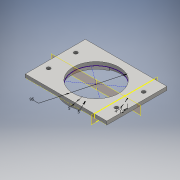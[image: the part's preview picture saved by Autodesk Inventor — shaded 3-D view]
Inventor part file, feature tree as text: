
AUTODESK INVENTOR PART (.ipt)
format: ipt  version: 2016 (Build 200138000, 138)  size: 188,928 bytes
history: native  units: mm
features: extrude x6, sketch x4, plane x2, other x1, revolve x1, chamfer x1, projected_geometry x1
ambient origin geometry x8: Origin, YZ Plane, XZ Plane, XY Plane, X Axis, Y Axis, Z Axis, Center Point
bodies: Solid1 (feature_tree)
feature tree (16):
  sketch  "Sketch1"  dims[d1=126.6mm d2=50.7mm]
  extrude  "Extrusion1"  Depth=50.7mm
  sketch  "Sketch4"  dims[d3=6.75mm d4=152.0mm]
  extrude  "Extrusion2"  Depth=152.0mm
  other  "Work Axis1"
  plane  "Work Plane3"
  revolve  "Revolution1"  [1 undecoded]
  plane  "Work Plane4"
  sketch  "Sketch7"  dims[d12=95.0mm d13=5.0mm d14=8.0mm d15=0.0mm d16=2.0mm d17=7.0mm d22=135.0deg d23=12.0mm d24=4.0mm d25=8.0mm d26=0.0mm d27=0.5mm d28=0.0mm d29=0.5mm d30=0.0mm d31=2.0mm d32=2.0mm d33=45.0deg d34=5.0mm d35=10.0mm d36=0.0mm]
  extrude  "Extrusion3"  Depth=10.0mm
  extrude  "Extrusion4"  Depth=8.0mm TaperAngle=0.0deg
  extrude  "Extrusion5"  Depth=2.0mm
  chamfer  "Chamfer1"  Distance=7.0mm
  extrude  "Extrusion6"  TaperAngle=135.0deg  [1 undecoded]
  sketch  "Sketch6"  dims[d5=112.0mm d6=6.5mm d7=0.0mm]
  projected_geometry  "Projected Loop4"
note: 2 required parameter values undecoded (feature->parameter linkage not recoverable at this tier; creation-order binding heuristic only, values carry confidence <= 0.55)